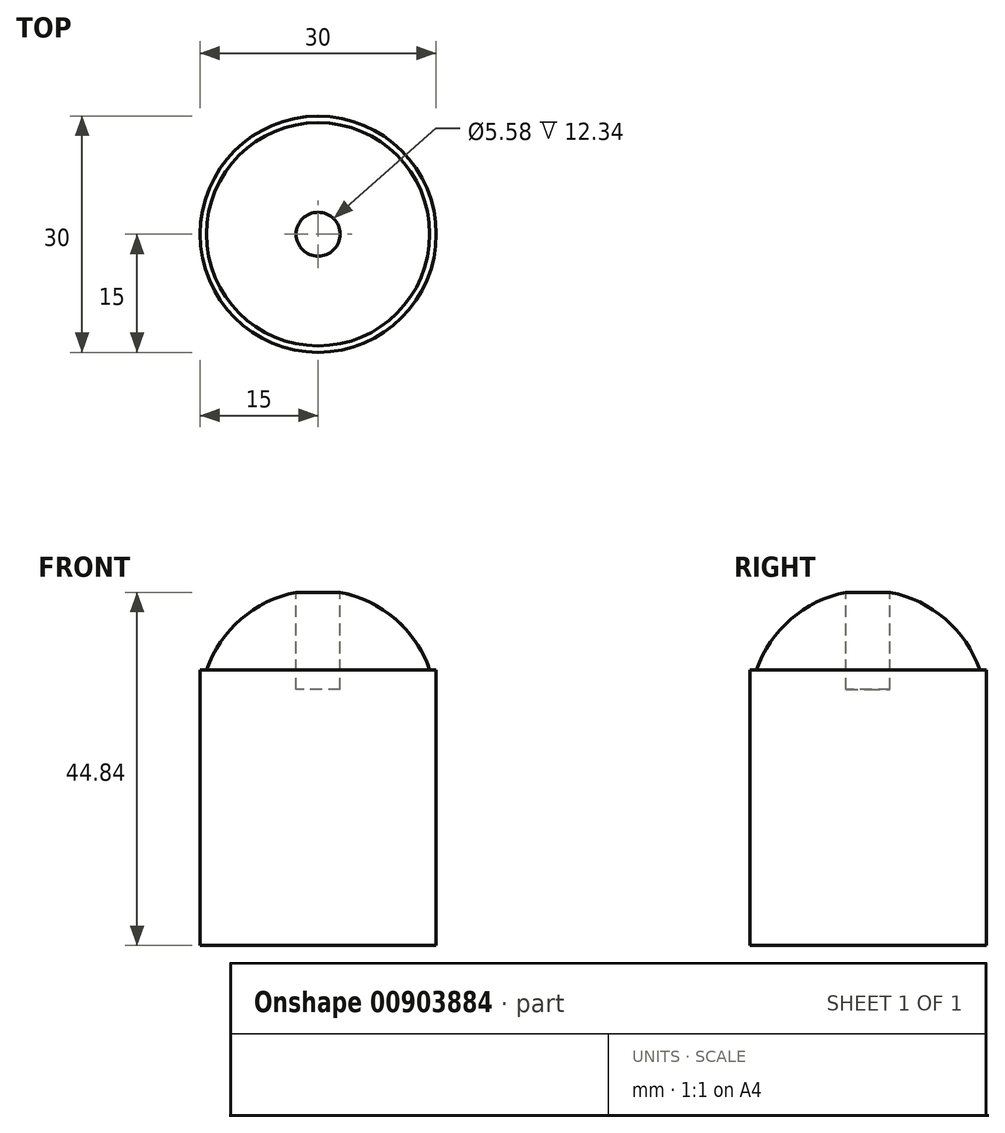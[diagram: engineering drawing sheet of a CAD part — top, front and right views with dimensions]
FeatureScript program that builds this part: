
annotation { "Feature Type Name" : "Feature", "Feature Type Description" : "" }
export const myFeature = defineFeature(function(context is Context, id is Id, definition is map)
    precondition{}
    {
        {
            var Q0;
            Q0=qCreatedBy(makeId("Top.planeOp"),FACE);
            var sketch = newSketch(context, id + "F0", { "sketchPlane" : qUnion([Q0])});
            skCircle(sketch, "E0", {"center": v(0, 0) * mm, "radius": 15 * mm});
            skSolve(sketch);
        }
        {
            var Q0;
            Q0 = qSketchRegion(id + "F0", true);
            extrude(context, id + "F1", {"entities" : qUnion([Q0]), "depth" : 35 * mm, "offsetDistance" : 25 * mm});
        }
        {
            var Q0;
            Q0=qCreatedBy(makeId("Front.planeOp"),FACE);
            var sketch = newSketch(context, id + "F2", { "sketchPlane" : qUnion([Q0])});
            skArc(sketch, "E1", {"start": v(0, 45.1) * mm, "mid": v(-10.66, 40.66) * mm, "end": v(-15, 29.95) * mm});
            skLineSegment(sketch, "E2", {"start": v(0, 45.1) * mm, "end": v(0, 15.1) * mm});
            skLineSegment(sketch, "E3", {"start": v(-15, 29.95) * mm, "end": v(15, 29.95) * mm});
            skSolve(sketch);
        }
        {
            var Q0;
            {var subQ0=sQuery(id+"F2.wireOp",EDGE,"E1");Q0=makeQuery(id+"F2.imprint","IMPRINT",FACE,{"disambiguationData":[TD([[makeQuery(id+"F2.imprint","IMPRINT",EDGE,{"derivedFrom":subQ0}),1.0]])]});}
            var Q1;
            Q1=sQuery(id+"F2.wireOp",EDGE,"E2");
            revolve(context, id + "F3", {"operationType" : NewBodyOperationType.ADD, "surfaceOperationType" : NewSurfaceOperationType.NEW, "entities" : qUnion([Q0]), "axis" : qUnion([Q1]), "revolveType" : RevolveType.FULL});
        }
        {
            var Q0;
            Q0=qCreatedBy(makeId("Top.planeOp"),FACE);
            cPlane(context, id + "F4", {"entities" : qUnion([Q0]), "cplaneType" : CPlaneType.OFFSET, "offset" : 52.5 * mm, "width" : 150 * mm, "height" : 150 * mm});
        }
        {
            var Q0;
            Q0=qCreatedBy(id+"F4.planeOp",FACE);
            var sketch = newSketch(context, id + "F5", { "sketchPlane" : qUnion([Q0])});
            skCircle(sketch, "E4", {"center": v(0, 0) * mm, "radius": 2.8 * mm});
            skSolve(sketch);
        }
        {
            var Q0;
            Q0 = qSketchRegion(id + "F5", true);
            extrude(context, id + "F6", {"entities" : qUnion([Q0]), "operationType" : NewBodyOperationType.REMOVE, "oppositeDirection" : true, "depth" : 20 * mm, "offsetDistance" : 25 * mm});
        }
    });
